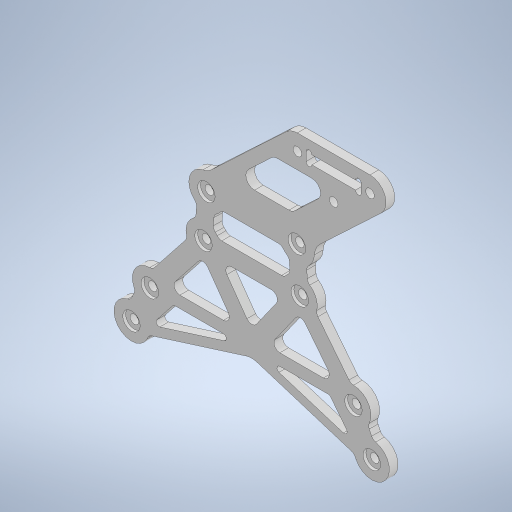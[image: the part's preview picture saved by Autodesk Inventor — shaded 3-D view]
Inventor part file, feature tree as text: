
AUTODESK INVENTOR PART (.ipt)
format: ipt  version: 2023.1 (Build 271208000, 208)  size: 475,648 bytes
history: native  units: mm
features: extrude x2, other x1
ambient origin geometry x8: Origin, YZ Plane, XZ Plane, XY Plane, X Axis, Y Axis, Z Axis, Center Point
bodies: Body1 (feature_tree)
feature tree (3):
  other  "ソリッド1"
  extrude  "押し出し1"  Depth=6.05mm
  extrude  "押し出し2"  Depth=6.05mm
